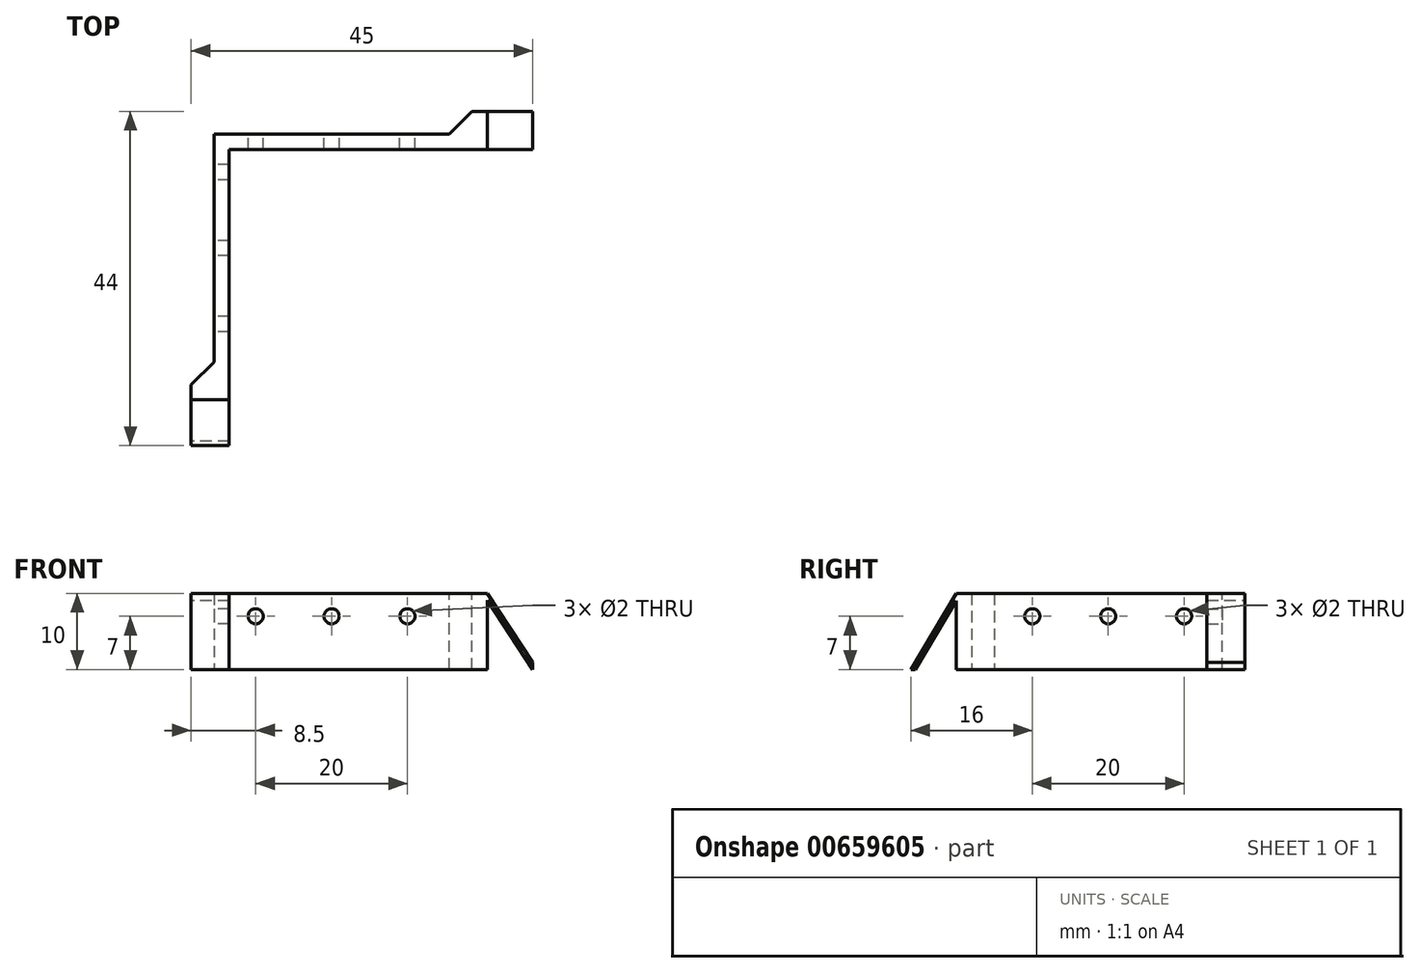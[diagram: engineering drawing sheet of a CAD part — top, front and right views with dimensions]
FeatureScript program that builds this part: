
annotation { "Feature Type Name" : "Feature", "Feature Type Description" : "" }
export const myFeature = defineFeature(function(context is Context, id is Id, definition is map)
    precondition{}
    {
        {
            var Q0;
            Q0=qCreatedBy(makeId("Top.planeOp"),FACE);
            var sketch = newSketch(context, id + "F0", { "sketchPlane" : qUnion([Q0])});
            skLineSegment(sketch, "E0.bottom", {"start": v(20, -19.5) * mm, "end": v(-20, -19.5) * mm});
            skLineSegment(sketch, "E0.top", {"start": v(20, 19.5) * mm, "end": v(-20, 19.5) * mm});
            skLineSegment(sketch, "E0.left", {"start": v(20, -19.5) * mm, "end": v(20, 19.5) * mm});
            skLineSegment(sketch, "E0.right", {"start": v(-20, -19.5) * mm, "end": v(-20, 19.5) * mm});
            skPoint(sketch, "E0.middle", {"position": v(0, 0) * mm});
            skLineSegment(sketch, "E1.0", {"start": v(22, -21.5) * mm, "end": v(-22, -21.5) * mm});
            skLineSegment(sketch, "E1.1", {"start": v(22, -21.5) * mm, "end": v(22, 21.5) * mm});
            skLineSegment(sketch, "E1.2", {"start": v(22, 21.5) * mm, "end": v(-22, 21.5) * mm});
            skLineSegment(sketch, "E1.3", {"start": v(-22, -21.5) * mm, "end": v(-22, 21.5) * mm});
            skLineSegment(sketch, "E2", {"start": v(-20, -19.5) * mm, "end": v(-22, -19.5) * mm});
            skLineSegment(sketch, "E3", {"start": v(20, 19.5) * mm, "end": v(20, 21.5) * mm});
            skSolve(sketch);
        }
        {
            var Q0;
            Q0=makeQuery(id+"F0.imprint","IMPRINT",FACE,{"disambiguationData":[TD([[makeQuery(id+"F0.imprint","IMPRINT",EDGE,{"derivedFrom":sQuery(id+"F0.wireOp",EDGE,"E0.top")}),-1.0]])]});
            var Q1;
            Q1=makeQuery(id+"F0.imprint","IMPRINT",FACE,{"disambiguationData":[TD([[makeQuery(id+"F0.imprint","IMPRINT",EDGE,{"derivedFrom":sQuery(id+"F0.wireOp",EDGE,"E0.bottom")}),1.0]])]});
            extrude(context, id + "F1", {"entities" : qUnion([Q0, Q1]), "oppositeDirection" : true, "depth" : 10 * mm, "offsetDistance" : 25 * mm});
        }
        {
            var Q0;
            Q0=makeQuery(id+"F1.opExtrude","SWEPT_FACE",FACE,{"disambiguationData":[OSD([sQuery(id+"F0.wireOp",EDGE,"E1.3")])]});
            var sketch = newSketch(context, id + "F2", { "sketchPlane" : qUnion([Q0])});
            skLineSegment(sketch, "E4", {"start": v(13.5, 0) * mm, "end": v(19.5, -10) * mm});
            skLineSegment(sketch, "E5", {"start": v(19.5, -10) * mm, "end": v(18.92, -10) * mm});
            skLineSegment(sketch, "E6", {"start": v(18.92, -10) * mm, "end": v(13.5, -0.97) * mm});
            skLineSegment(sketch, "E7", {"start": v(13.5, -0.97) * mm, "end": v(13.5, -10) * mm});
            skLineSegment(sketch, "E8", {"start": v(19.5, -10) * mm, "end": v(19.5, 0) * mm});
            skLineSegment(sketch, "E9", {"start": v(19.5, 0) * mm, "end": v(13.5, 0) * mm});
            skSolve(sketch);
        }
        {
            var Q0;
            {var subQ0=sQuery(id+"F2.wireOp",EDGE,"E6");Q0=makeQuery(id+"F2.imprint","IMPRINT",FACE,{"disambiguationData":[TD([[makeQuery(id+"F2.imprint","IMPRINT",EDGE,{"derivedFrom":subQ0}),1.0]])]});}
            extrude(context, id + "F3", {"entities" : qUnion([Q0]), "operationType" : NewBodyOperationType.REMOVE, "oppositeDirection" : true, "depth" : 25 * mm, "offsetDistance" : 25 * mm});
        }
        {
            var Q0;
            Q0=makeQuery(id+"F2.imprint","IMPRINT",FACE,{"disambiguationData":[TD([[makeQuery(id+"F2.imprint","IMPRINT",EDGE,{"derivedFrom":sQuery(id+"F2.wireOp",EDGE,"E4")}),1.0]])]});
            extrude(context, id + "F4", {"entities" : qUnion([Q0]), "operationType" : NewBodyOperationType.REMOVE, "endBound" : BoundingType.THROUGH_ALL, "oppositeDirection" : true, "depth" : 2 * mm, "offsetDistance" : 25 * mm});
        }
        {
            var Q0;
            Q0=makeQuery(id+"F1.opExtrude","SWEPT_FACE",FACE,{"disambiguationData":[OSD([sQuery(id+"F0.wireOp",EDGE,"E1.2")])]});
            var sketch = newSketch(context, id + "F5", { "sketchPlane" : qUnion([Q0])});
            skLineSegment(sketch, "E10", {"start": v(-20, -10) * mm, "end": v(-14, -0.9) * mm});
            skLineSegment(sketch, "E11", {"start": v(-14, -0.9) * mm, "end": v(-14, -10) * mm});
            skLineSegment(sketch, "E12", {"start": v(-14, 0) * mm, "end": v(-20, -9.1) * mm});
            skLineSegment(sketch, "E13", {"start": v(-20, -9.1) * mm, "end": v(-20, -10) * mm});
            skSolve(sketch);
        }
        {
            var Q0;
            {var subQ0=sQuery(id+"F5.wireOp",EDGE,"E10");Q0=makeQuery(id+"F5.imprint","IMPRINT",FACE,{"disambiguationData":[TD([[makeQuery(id+"F5.imprint","IMPRINT",EDGE,{"derivedFrom":subQ0}),-1.0]])]});}
            var Q1;
            {var subQ3=sQuery(id+"F5.wireOp",EDGE,"E12");Q1=makeQuery(id+"F5.imprint","IMPRINT",FACE,{"disambiguationData":[TD([[makeQuery(id+"F5.imprint","IMPRINT",EDGE,{"derivedFrom":subQ3}),-1.0]])]});}
            extrude(context, id + "F6", {"entities" : qUnion([Q0, Q1]), "operationType" : NewBodyOperationType.REMOVE, "endBound" : BoundingType.THROUGH_ALL, "oppositeDirection" : true, "depth" : 25 * mm, "offsetDistance" : 25 * mm});
        }
        {
            var Q0;
            {var subQ0=sQuery(id+"F0.wireOp",EDGE,"E1.3");var subQ7=sQuery(id+"F0.wireOp",EDGE,"E0.bottom");Q0=makeQuery(id+"F4.boolean.opBoolean","SPLIT",FACE,{"disambiguationData":[TD([makeQuery(id+"F1.opExtrude","SWEPT_FACE",FACE,{"disambiguationData":[OSD([subQ7])]})])],"derivedFrom":makeQuery(id+"F1.opExtrude","SWEPT_FACE",FACE,{"disambiguationData":[OSD([subQ0])]})});}
            extrude(context, id + "F7", {"entities" : qUnion([Q0]), "operationType" : NewBodyOperationType.REMOVE, "endBound" : BoundingType.THROUGH_ALL, "oppositeDirection" : true, "depth" : 25 * mm, "offsetDistance" : 25 * mm});
        }
        {
            var Q0;
            Q0=makeQuery(id+"F1.opExtrude","SWEPT_FACE",FACE,{"disambiguationData":[OSD([sQuery(id+"F0.wireOp",EDGE,"E1.2")])]});
            var sketch = newSketch(context, id + "F8", { "sketchPlane" : qUnion([Q0])});
            skLineSegment(sketch, "E14", {"start": v(-9, -10) * mm, "end": v(-9, 0) * mm});
            skSolve(sketch);
        }
        {
            var Q0;
            {var subQ2=sQuery(id+"F8.wireOp",EDGE,"E14");Q0=makeQuery(id+"F8.imprint","IMPRINT",FACE,{"disambiguationData":[TD([[makeQuery(id+"F8.imprint","IMPRINT",EDGE,{"derivedFrom":subQ2}),1.0]])]});}
            extrude(context, id + "F9", {"entities" : qUnion([Q0]), "operationType" : NewBodyOperationType.ADD, "depth" : 3 * mm, "offsetDistance" : 25 * mm});
        }
        {
            var Q0;
            Q0=makeQuery(id+"F9.opExtrude","CAP_EDGE",EDGE,{"disambiguationData":[OSD([sQuery(id+"F8.wireOp",EDGE,"E14")])],"isStart":false});
            chamfer(context, id + "F10", {"entities" : qUnion([Q0]), "width" : 3 * mm, "tangentPropagation" : true});
        }
        {
            var Q0;
            {var subQ0=sQuery(id+"F0.wireOp",EDGE,"E1.2");var subQ1=sQuery(id+"F0.wireOp",EDGE,"E1.3");Q0=makeQuery(id+"F4.boolean.opBoolean","SPLIT",FACE,{"disambiguationData":[TD([makeQuery(id+"F1.opExtrude","SWEPT_FACE",FACE,{"disambiguationData":[OSD([subQ0])]})])],"derivedFrom":makeQuery(id+"F1.opExtrude","SWEPT_FACE",FACE,{"disambiguationData":[OSD([subQ1])]})});}
            var sketch = newSketch(context, id + "F11", { "sketchPlane" : qUnion([Q0])});
            skLineSegment(sketch, "E15", {"start": v(8.5, 0) * mm, "end": v(8.5, -10) * mm});
            skSolve(sketch);
        }
        {
            var Q0;
            {var subQ5=sQuery(id+"F11.wireOp",EDGE,"E15");Q0=makeQuery(id+"F11.imprint","IMPRINT",FACE,{"disambiguationData":[TD([[makeQuery(id+"F11.imprint","IMPRINT",EDGE,{"derivedFrom":subQ5}),1.0]])]});}
            extrude(context, id + "F12", {"entities" : qUnion([Q0]), "operationType" : NewBodyOperationType.ADD, "depth" : 3 * mm, "offsetDistance" : 25 * mm});
        }
        {
            var Q0;
            Q0=makeQuery(id+"F12.opExtrude","CAP_EDGE",EDGE,{"disambiguationData":[OSD([sQuery(id+"F11.wireOp",EDGE,"E15")])],"isStart":false});
            chamfer(context, id + "F13", {"entities" : qUnion([Q0]), "width" : 3 * mm, "tangentPropagation" : true});
        }
        {
            var Q0;
            {var subQ0=sQuery(id+"F0.wireOp",EDGE,"E1.2");var subQ1=sQuery(id+"F0.wireOp",EDGE,"E1.3");Q0=makeQuery(id+"F4.boolean.opBoolean","SPLIT",FACE,{"disambiguationData":[TD([makeQuery(id+"F1.opExtrude","SWEPT_FACE",FACE,{"disambiguationData":[OSD([subQ0])]})])],"derivedFrom":makeQuery(id+"F1.opExtrude","SWEPT_FACE",FACE,{"disambiguationData":[OSD([subQ1])]})});}
            var sketch = newSketch(context, id + "F14", { "sketchPlane" : qUnion([Q0])});
            skLineSegment(sketch, "E16", {"start": v(-6.5, -10) * mm, "end": v(-6.5, -3) * mm, "construction": true});
            skPoint(sketch, "E16.endSnap0", {"position": v(-6.5, -10) * mm});
            skLineSegment(sketch, "E17", {"start": v(-6.5, -3) * mm, "end": v(3.5, -3) * mm, "construction": true});
            skLineSegment(sketch, "E18", {"start": v(-6.5, -3) * mm, "end": v(-16.5, -3) * mm, "construction": true});
            skSolve(sketch);
        }
        {
            var Q0;
            Q0=makeQuery(id+"F1.opExtrude","SWEPT_FACE",FACE,{"disambiguationData":[OSD([sQuery(id+"F0.wireOp",EDGE,"E1.2")])]});
            var sketch = newSketch(context, id + "F15", { "sketchPlane" : qUnion([Q0])});
            skLineSegment(sketch, "E19", {"start": v(6.5, -3) * mm, "end": v(16.5, -3) * mm, "construction": true});
            skPoint(sketch, "E19.startSnap0", {"position": v(6.5, -10) * mm});
            skLineSegment(sketch, "E20", {"start": v(6.5, -3) * mm, "end": v(-3.5, -3) * mm, "construction": true});
            skLineSegment(sketch, "E21", {"start": v(6.5, -3) * mm, "end": v(6.5, -10) * mm, "construction": true});
            skSolve(sketch);
        }
        {
            var Q0;
            Q0=sQuery(id+"F14.wireOp",VERTEX,"E18.start");
            var Q1;
            Q1=sQuery(id+"F14.wireOp",VERTEX,"E17.end");
            var Q2;
            Q2=sQuery(id+"F14.wireOp",VERTEX,"E18.end");
            var Q3;
            Q3=makeQuery(id+"F4.boolean.opBoolean","SPLIT",BODY,{"disambiguationData":[OD(1.0)],"derivedFrom":makeQuery(id+"F1.opExtrude","SWEPT_BODY",BODY,{"disambiguationData":[OSD([sQuery(id+"F0.wireOp",EDGE,"E0.bottom"),sQuery(id+"F0.wireOp",EDGE,"E0.top"),sQuery(id+"F0.wireOp",EDGE,"E0.left"),sQuery(id+"F0.wireOp",EDGE,"E0.right"),sQuery(id+"F0.wireOp",EDGE,"E1.0"),sQuery(id+"F0.wireOp",EDGE,"E1.1"),sQuery(id+"F0.wireOp",EDGE,"E1.2"),sQuery(id+"F0.wireOp",EDGE,"E1.3")])]})});
            hole(context, id + "F16", {"style" : HoleStyle.SIMPLE, "endStyle" : HoleEndStyle.THROUGH, "holeDiameter" : 2 * mm, "majorDiameter" : 5 * mm, "isTappedThrough" : true, "tappedDepth" : 12 * mm, "tapClearance" : 3, "locations" : qUnion([Q0, Q1, Q2]), "scope" : qUnion([Q3])});
        }
        {
            var Q0;
            Q0=sQuery(id+"F15.wireOp",VERTEX,"E20.end");
            var Q1;
            Q1=sQuery(id+"F15.wireOp",VERTEX,"E19.start");
            var Q2;
            Q2=sQuery(id+"F15.wireOp",VERTEX,"E19.end");
            var Q3;
            Q3=makeQuery(id+"F4.boolean.opBoolean","SPLIT",BODY,{"disambiguationData":[OD(1.0)],"derivedFrom":makeQuery(id+"F1.opExtrude","SWEPT_BODY",BODY,{"disambiguationData":[OSD([sQuery(id+"F0.wireOp",EDGE,"E0.bottom"),sQuery(id+"F0.wireOp",EDGE,"E0.top"),sQuery(id+"F0.wireOp",EDGE,"E0.left"),sQuery(id+"F0.wireOp",EDGE,"E0.right"),sQuery(id+"F0.wireOp",EDGE,"E1.0"),sQuery(id+"F0.wireOp",EDGE,"E1.1"),sQuery(id+"F0.wireOp",EDGE,"E1.2"),sQuery(id+"F0.wireOp",EDGE,"E1.3")])]})});
            hole(context, id + "F17", {"style" : HoleStyle.SIMPLE, "endStyle" : HoleEndStyle.THROUGH, "holeDiameter" : 2 * mm, "majorDiameter" : 5 * mm, "isTappedThrough" : true, "tappedDepth" : 12 * mm, "tapClearance" : 3, "locations" : qUnion([Q0, Q1, Q2]), "scope" : qUnion([Q3])});
        }
    });
